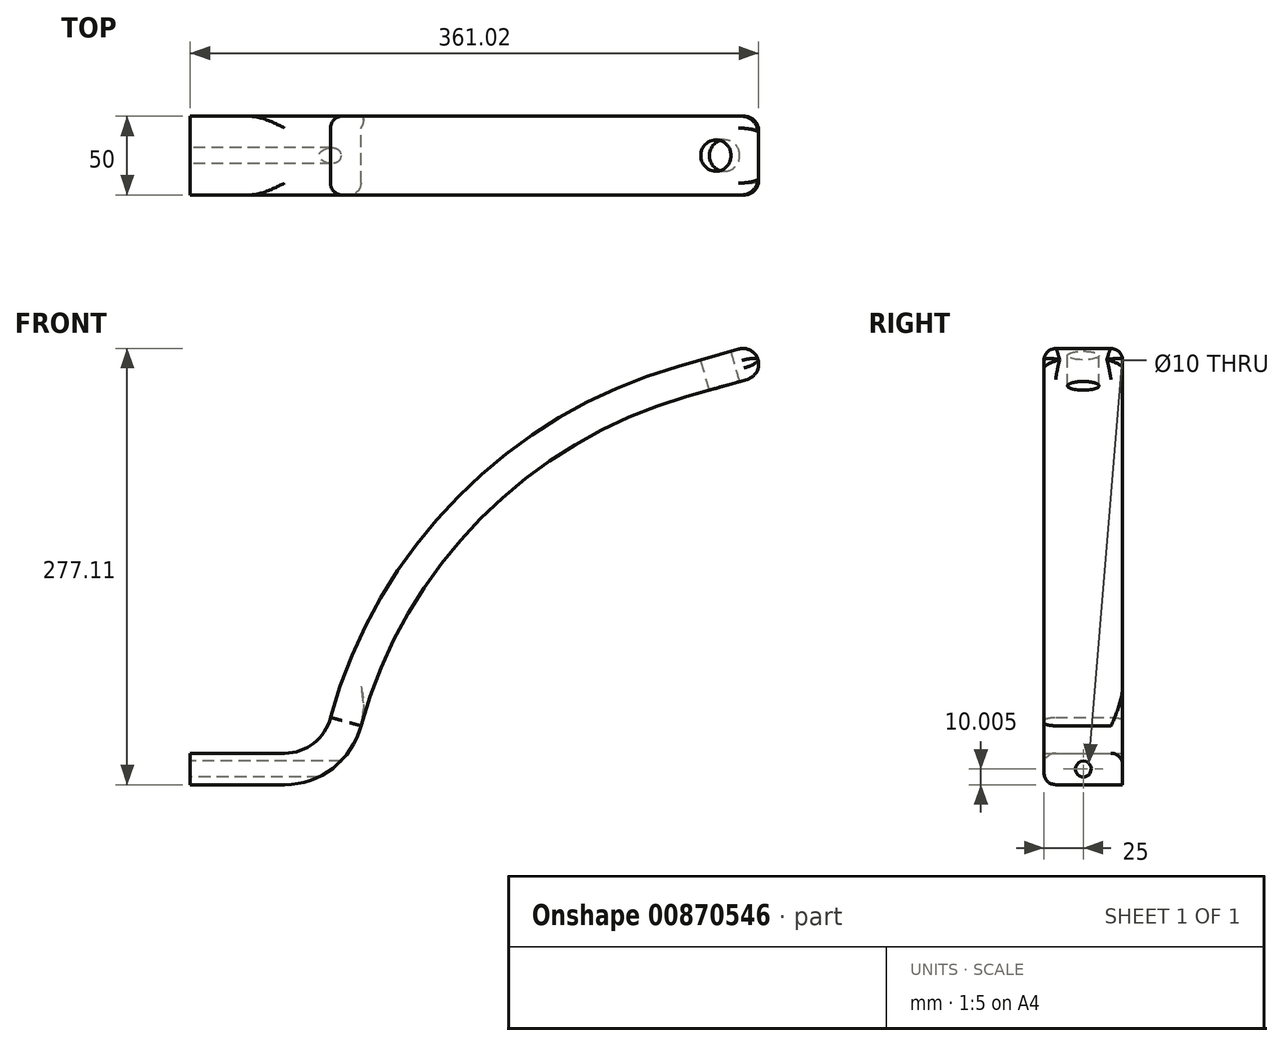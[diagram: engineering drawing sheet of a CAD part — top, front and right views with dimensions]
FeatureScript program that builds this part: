
annotation { "Feature Type Name" : "Feature", "Feature Type Description" : "" }
export const myFeature = defineFeature(function(context is Context, id is Id, definition is map)
    precondition{}
    {
        {
            var Q0;
            Q0=qCreatedBy(makeId("Front.planeOp"),FACE);
            var sketch = newSketch(context, id + "F0", { "sketchPlane" : qUnion([Q0])});
            skArc(sketch, "E0", {"start": v(-82.4, 288.46) * mm, "mid": v(-213.22, 211.04) * mm, "end": v(-289.3, 79.41) * mm});
            skArc(sketch, "E1", {"start": v(-87.88, 307.7) * mm, "mid": v(-227.44, 225.1) * mm, "end": v(-308.59, 84.7) * mm});
            skLineSegment(sketch, "E2", {"start": v(-82.4, 288.46) * mm, "end": v(-34.31, 302.2) * mm});
            skLineSegment(sketch, "E3", {"start": v(-34.31, 302.2) * mm, "end": v(-39.8, 321.43) * mm});
            skLineSegment(sketch, "E4", {"start": v(-39.8, 321.43) * mm, "end": v(-87.88, 307.7) * mm});
            skArc(sketch, "E5", {"start": v(-337.7, 61.96) * mm, "mid": v(-319.23, 68.32) * mm, "end": v(-308.59, 84.7) * mm});
            skArc(sketch, "E6", {"start": v(-337.7, 41.96) * mm, "mid": v(-307.1, 52.42) * mm, "end": v(-289.3, 79.41) * mm});
            skLineSegment(sketch, "E7.top", {"start": v(-337.7, 41.96) * mm, "end": v(-397.7, 41.96) * mm});
            skLineSegment(sketch, "E7.right", {"start": v(-397.7, 61.96) * mm, "end": v(-397.7, 41.96) * mm});
            skLineSegment(sketch, "E8", {"start": v(-397.7, 61.96) * mm, "end": v(-337.7, 61.96) * mm});
            skSolve(sketch);
        }
        {
            var Q0;
            Q0=makeQuery(id+"F0.imprint","IMPRINT",FACE,{"disambiguationData":[TD([[makeQuery(id+"F0.imprint","IMPRINT",EDGE,{"derivedFrom":sQuery(id+"F0.wireOp",EDGE,"E0")}),-1.0]])]});
            extrude(context, id + "F1", {"entities" : qUnion([Q0]), "depth" : 50 * mm, "offsetDistance" : 25 * mm});
        }
        {
            var Q0;
            Q0=makeQuery(id+"F1.opExtrude","SWEPT_FACE",FACE,{"disambiguationData":[OSD([sQuery(id+"F0.wireOp",EDGE,"E4")])]});
            var sketch = newSketch(context, id + "F2", { "sketchPlane" : qUnion([Q0])});
            skPoint(sketch, "E9", {"position": v(25, -25) * mm});
            skPoint(sketch, "E9.positionSnap0", {"position": v(50, -25) * mm});
            skSolve(sketch);
        }
        {
            var Q0;
            Q0=sQuery(id+"F2.wireOp",VERTEX,"E9");
            var Q1;
            Q1=makeQuery(id+"F1.opExtrude","SWEPT_BODY",BODY,{"disambiguationData":[OSD([sQuery(id+"F0.wireOp",EDGE,"E0"),sQuery(id+"F0.wireOp",EDGE,"E1"),sQuery(id+"F0.wireOp",EDGE,"E2"),sQuery(id+"F0.wireOp",EDGE,"E3"),sQuery(id+"F0.wireOp",EDGE,"E4"),sQuery(id+"F0.wireOp",EDGE,"E6"),sQuery(id+"F0.wireOp",EDGE,"E7.top"),sQuery(id+"F0.wireOp",EDGE,"E7.right"),sQuery(id+"F0.wireOp",EDGE,"E8"),sQuery(id+"F0.wireOp",EDGE,"E5")])]});
            hole(context, id + "F3", {"style" : HoleStyle.SIMPLE, "endStyle" : HoleEndStyle.THROUGH, "holeDiameter" : 20 * mm, "majorDiameter" : 5 * mm, "isTappedThrough" : true, "tappedDepth" : 12 * mm, "tapClearance" : 3, "locations" : qUnion([Q0]), "scope" : qUnion([Q1])});
        }
        {
            var Q0;
            Q0=makeQuery(id+"F1.opExtrude","SWEPT_FACE",FACE,{"disambiguationData":[OSD([sQuery(id+"F0.wireOp",EDGE,"E7.right")])]});
            var sketch = newSketch(context, id + "F4", { "sketchPlane" : qUnion([Q0])});
            skPoint(sketch, "E10", {"position": v(25, 51.96) * mm});
            skCircle(sketch, "E11", {"center": v(25, 51.96) * mm, "radius": 5 * mm});
            skSolve(sketch);
        }
        {
            var Q0;
            Q0=sQuery(id+"F4.wireOp",VERTEX,"E10");
            var Q1;
            Q1=makeQuery(id+"F1.opExtrude","SWEPT_BODY",BODY,{"disambiguationData":[OSD([sQuery(id+"F0.wireOp",EDGE,"E0"),sQuery(id+"F0.wireOp",EDGE,"E1"),sQuery(id+"F0.wireOp",EDGE,"E2"),sQuery(id+"F0.wireOp",EDGE,"E3"),sQuery(id+"F0.wireOp",EDGE,"E4"),sQuery(id+"F0.wireOp",EDGE,"E6"),sQuery(id+"F0.wireOp",EDGE,"E7.top"),sQuery(id+"F0.wireOp",EDGE,"E7.right"),sQuery(id+"F0.wireOp",EDGE,"E8"),sQuery(id+"F0.wireOp",EDGE,"E5")])]});
            hole(context, id + "F5", {"style" : HoleStyle.SIMPLE, "endStyle" : HoleEndStyle.THROUGH, "holeDiameter" : 10 * mm, "majorDiameter" : 5 * mm, "isTappedThrough" : true, "tappedDepth" : 12 * mm, "tapClearance" : 3, "locations" : qUnion([Q0]), "scope" : qUnion([Q1])});
        }
        {
            var Q0;
            Q0=makeQuery(id+"F1.opExtrude","CAP_EDGE",EDGE,{"disambiguationData":[OSD([sQuery(id+"F0.wireOp",EDGE,"E1")])],"isStart":false});
            var Q1;
            Q1=makeQuery(id+"F1.opExtrude","CAP_EDGE",EDGE,{"disambiguationData":[OSD([sQuery(id+"F0.wireOp",EDGE,"E0")])],"isStart":false});
            var Q2;
            Q2=makeQuery(id+"F1.opExtrude","CAP_EDGE",EDGE,{"disambiguationData":[OSD([sQuery(id+"F0.wireOp",EDGE,"E6")])],"isStart":false});
            fillet(context, id + "F6", {"entities" : qUnion([Q0, Q1, Q2]), "radius" : 7.5 * mm, "tangentPropagation" : true, "allowEdgeOverflow" : false});
        }
        {
            var Q0;
            Q0=makeQuery(id+"F1.opExtrude","CAP_EDGE",EDGE,{"disambiguationData":[OSD([sQuery(id+"F0.wireOp",EDGE,"E1")])],"isStart":true});
            var Q1;
            Q1=makeQuery(id+"F1.opExtrude","CAP_EDGE",EDGE,{"disambiguationData":[OSD([sQuery(id+"F0.wireOp",EDGE,"E0")])],"isStart":true});
            fillet(context, id + "F7", {"entities" : qUnion([Q0, Q1]), "radius" : 7.5 * mm, "tangentPropagation" : true, "allowEdgeOverflow" : false});
        }
        {
            var Q0;
            Q0=makeQuery(id+"F1.opExtrude","SWEPT_EDGE",EDGE,{"disambiguationData":[OSD([sQuery(id+"F0.wireOp",EDGE,"E3"),sQuery(id+"F0.wireOp",EDGE,"E4")])]});
            fillet(context, id + "F8", {"entities" : qUnion([Q0]), "radius" : 10 * mm, "tangentPropagation" : true, "allowEdgeOverflow" : false});
        }
    });
